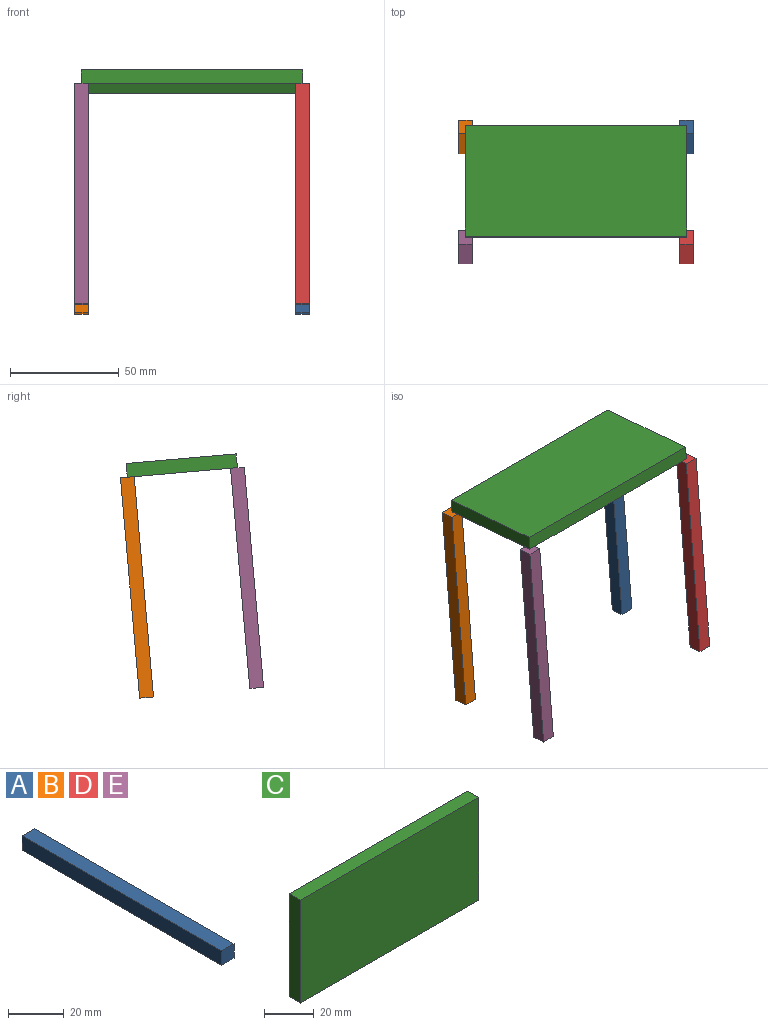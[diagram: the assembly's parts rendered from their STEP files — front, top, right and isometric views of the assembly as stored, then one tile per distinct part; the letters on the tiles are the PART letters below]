
ASSEMBLY  parts=5 mates=4
PART A: 6 faces, bbox 6.4x101.6x6.4 mm
  f0: plane 101.6x6.35mm, normal (-1,0,0), area 645.2mm2, adj f1,f3,f4,f5
  f1: plane 101.6x6.35mm, normal (0,0,-1), area 645.2mm2, adj f0,f2,f4,f5
  f2: plane 101.6x6.35mm, normal (1,0,0), area 645.2mm2, adj f1,f3,f4,f5
  f3: plane 101.6x6.35mm, normal (0,0,1), area 645.2mm2, adj f0,f2,f4,f5
  f4: plane 6.35x6.35mm, normal (0,1,0), area 40.3mm2, adj f0,f1,f2,f3
  f5: plane 6.35x6.35mm, normal (0,-1,0), area 40.3mm2, adj f0,f1,f2,f3
PART B: same geometry as A
PART C: 6 faces, bbox 101.6x6.4x50.8 mm
  f0: plane 50.8x6.35mm, normal (-1,0,0), area 322.6mm2, adj f1,f3,f4,f5
  f1: plane 101.6x6.35mm, normal (0,0,-1), area 645.2mm2, adj f0,f2,f4,f5
  f2: plane 50.8x6.35mm, normal (1,0,0), area 322.6mm2, adj f1,f3,f4,f5
  f3: plane 101.6x6.35mm, normal (0,0,1), area 645.2mm2, adj f0,f2,f4,f5
  f4: plane 101.6x50.8mm, normal (0,-1,0), area 5161.3mm2, adj f0,f1,f2,f3
  f5: plane 101.6x50.8mm, normal (0,1,0), area 5161.3mm2, adj f0,f1,f2,f3
PART D: same geometry as A
PART E: same geometry as A
PLACE A rot(axis=(-1,0,0),95deg) t=(-6.88,44.02,9.31)mm
PLACE B rot(axis=(-1,0,0),95deg) t=(-108.48,44.02,9.31)mm
PLACE C rot(axis=(-1,0,0),95deg) t=(-57.68,18.71,11.52)mm
PLACE D rot(axis=(-1,0,0),95deg) t=(-6.88,-6.59,13.74)mm
PLACE E rot(axis=(-1,0,0),95deg) t=(-108.48,-6.59,13.74)mm
MATE fastened A.f5 <-> C.f5  axis (0,0.09,1) through (-6.88,44.02,9.31)mm
MATE fastened B.f5 <-> C.f5  axis (0,0.09,1) through (-108.48,44.02,9.31)mm
MATE fastened E.f5 <-> C.f5  axis (0,0.09,1) through (-108.48,-6.59,13.74)mm
MATE fastened D.f5 <-> C.f5  axis (0,0.09,1) through (-6.88,-6.59,13.74)mm
